# Revit family: 01622196
name_source: partatom
category: Plumbing Fixtures
revit_build: Autodesk Revit 2018 (Build: 20170223_1515(x64)
units: mm (PartAtom-declared; Revit-internal decimal feet)

## family parameters
Always vertical = Yes
Cut with Voids When Loaded = No
OmniClass Number = 23.45.55.00
OmniClass Title = Sanitary Faucets, Wastes
Part Type = Normal
Room Calculation Point = No
Round Connector Dimension = Use Diameter
Shared = No
Work Plane-Based = No

## types (1)
- 01622196 Washbasin faucet
    2D/3D/BIM Files URL = http://static.hansa.com
    3D View = https://static.hansa.com
    Advanced Features = Waterways without nickel coating;Surfaces in contact with drinking water contain less than 0.3% lead;Inner body made of DZR brass;Rapid installation system
    Aerator = Laminar stream
    Ambience photo = http://static.hansa.com
    Approval ABP = P-IX 29891/IA
    Approval DVGW = NW-6506CR0028
    AssetType = Fixed
    BIMObjectName = 01622196
    Backflow Prevention EN1717 = AA
    BodyMaterial = Brass
    Brand = HANSA
    Catalog Drawing URL = http://static.hansa.com
    Category = Health & Care
    CloseOffRating = 0
    Color = Chrome
    Connection = Copper inlet pipes
    Connection Size = Ø10
    Dimension Drawing URL = http://static.hansa.com
    DurationUnit = Year
    EAN Number = 4015474267039
    EN Standard = EN 817
    ETIM Class Number = EC011328 Washbasin mixing tap
    Excluded Items = Without pop-up waste;Without draw-rod opening
    FDV Document URL = http://www.hansa.com
    FaucetMainMaterial = Brass
    Features = Single-lever
    Finish = Polished
    Flow Drawing URL = http://static.hansa.com
    Flow Rate At 300kPa = 0.2 L/s
    FlowCoefficient = 0
    Group = Washbasin faucet
    IfcExportAs = IfcValveType
    IfcExportType = FAUCET
    InletConnectionSize = 10 mm  [stored 0.0328084 ft]
    Installation Type = Deck mounted
    Installation and Maintenance Guide URL = http://static.hansa.com
    Interactive AR View URL = https://static.hansa.com
    Lever Handle = Long shape;Hot/Cold symbols;Single operating lever/handle
    Manufacturer = HANSA
    ManufacturerName = HANSA
    ManufacturerURL = http://www.hansa.com
    Market = Austria;Belgium;Czech Republic;Germany;Spain;France;International;Italy;Netherlands;Slovakia
    Material = Brass
    Max. Hot Water Supply = 80 °C
    Mechanical Parts = ø 48 mm ceramic cartridge for flow and temperature control
    Mechanical parts = 48 Cartridge
    Mobile Product Information URL = http://mpi.hansa.com
    Model = 01622196 Washbasin faucet
    ModelReference = 01622196
    Mounting Holes = 1 hole
    NBSDescription = Water supply fittings for wash basins and troughs
    NBSReference = 45-35-70/371
    Name = 01622196 Washbasin faucet
    Name_en = 01622196 Washbasin faucet
    Noise Class = I (ISO 3822)
    NominalDepth = 173 mm
    NominalHeight = 199 mm  [stored 0.652887 ft]
    NominalWidth = 58 mm  [stored 0.190289 ft]
    Product Code = 01622196
    Product Family = HANSAMEDIPRO Protec
    Product Image URL = http://static.hansa.com
    Product URL = http://static.hansa.com
    Revision = 4
    Sales Package dimensions (LxWxH) = 606 x 224 x 88
    Shape = Sculptured
    Size = 58x172,5x199 mm
    Spare-Part Information URL = http://static.hansa.com
    Special Features = Waterways without nickel, leadfree
    Spout Projection = 120 mm
    Spout Type = Fixed spout
    Surface treatment = Chrome
    Technical DataSheet URL = http://www.hansa.com
    Temperature = Temperature limiter;Temperature limiter (retrofittable)
    Temperature Adjustments = Limitation option for maximum temperature and flow-rate ;Adjustable hot water stop (included, retrofittable)
    UNSPSC Class Number = 30181700 Faucets or taps
    URL ABP = http://static.hansa.com
    URL DVGW = http://static.hansa.com
    URL Declaration of Conformity = http://static.hansa.com
    URL REACH = http://static.hansa.com
    Uniclass2 = Pr_40_30_96_96
    Uniclass2015Description = Washbasin manual water supply sets
    Uniclass2015Reference = Pr_40_20_87_96
    Version = 4
    VersionDate = 01/07/2022
    Warranty Information URL = http://warranty.hansa.com
    WarrantyDescription = http://warranty.hansa.com
    WarrantyDurationUnit = Year
    Working Pressure = 50 - 1000 kPa
    WorkingPressure = 50 - 1000 kPa

note: [stored X ft] marks values corroborated as IEEE doubles in the binary element streams (Revit-internal decimal feet)

## geometry (parser evidence)
native form markers: Sweep x4
no freeform markers — native parametric forms only
